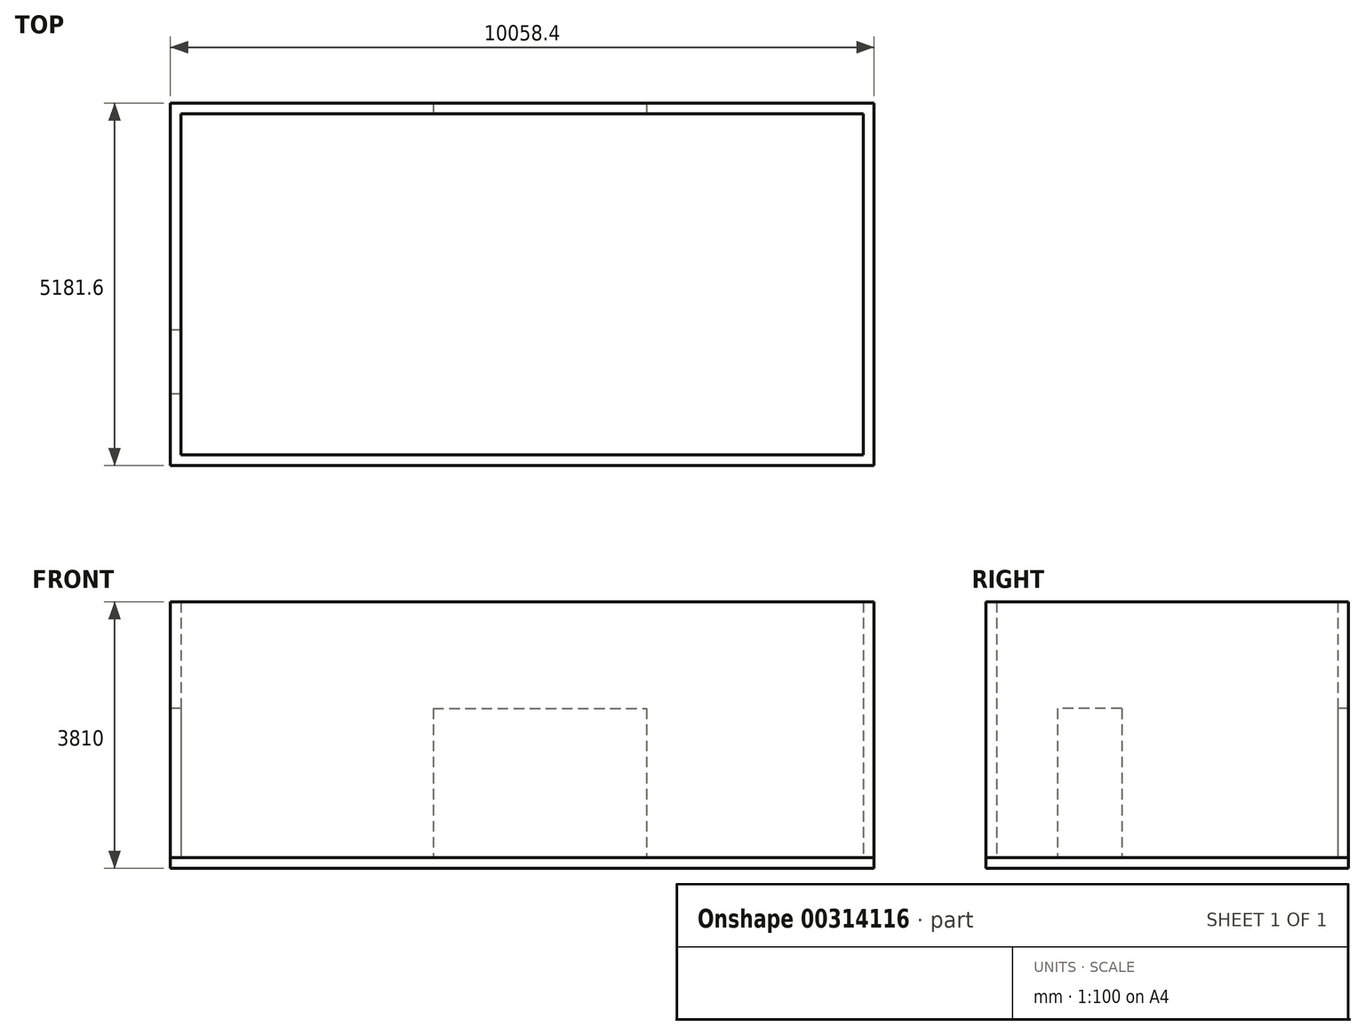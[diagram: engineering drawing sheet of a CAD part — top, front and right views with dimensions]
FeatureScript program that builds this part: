
annotation { "Feature Type Name" : "Feature", "Feature Type Description" : "" }
export const myFeature = defineFeature(function(context is Context, id is Id, definition is map)
    precondition{}
    {
        {
            var Q0;
            Q0=qCreatedBy(makeId("Top.planeOp"),FACE);
            var sketch = newSketch(context, id + "F0", { "sketchPlane" : qUnion([Q0])});
            skLineSegment(sketch, "E0.bottom", {"start": v(-2518.32, 3830.27) * mm, "end": v(7235.28, 3830.27) * mm});
            skLineSegment(sketch, "E0.top", {"start": v(-2518.32, -1046.53) * mm, "end": v(7235.28, -1046.53) * mm});
            skLineSegment(sketch, "E0.left", {"start": v(-2518.32, 3830.27) * mm, "end": v(-2518.32, -1046.53) * mm});
            skLineSegment(sketch, "E0.right", {"start": v(7235.28, 3830.27) * mm, "end": v(7235.28, -1046.53) * mm});
            skLineSegment(sketch, "E1.0", {"start": v(-2670.72, 3982.67) * mm, "end": v(-2670.72, -1198.93) * mm});
            skLineSegment(sketch, "E1.1", {"start": v(-2670.72, 3982.67) * mm, "end": v(7387.68, 3982.67) * mm});
            skLineSegment(sketch, "E1.2", {"start": v(7387.68, 3982.67) * mm, "end": v(7387.68, -1198.93) * mm});
            skLineSegment(sketch, "E1.3", {"start": v(-2670.72, -1198.93) * mm, "end": v(7387.68, -1198.93) * mm});
            skLineSegment(sketch, "E2", {"start": v(-2518.32, 738.17) * mm, "end": v(-2670.72, 738.17) * mm});
            skLineSegment(sketch, "E3", {"start": v(-2518.32, -176.23) * mm, "end": v(-2670.72, -176.23) * mm});
            skLineSegment(sketch, "E4", {"start": v(4132.59, 3982.67) * mm, "end": v(4132.59, 3830.27) * mm});
            skLineSegment(sketch, "E5", {"start": v(1084.59, 3982.67) * mm, "end": v(1084.59, 3830.27) * mm});
            skSolve(sketch);
        }
        {
            var Q0;
            Q0 = qSketchRegion(id + "F0", true);
            extrude(context, id + "F1", {"entities" : qUnion([Q0]), "depth" : 3657.6 * mm});
        }
        {
            var Q0;
            {var subQ0=sQuery(id+"F0.wireOp",EDGE,"E4");Q0=makeQuery(id+"F0.imprint","IMPRINT",FACE,{"disambiguationData":[TD([[makeQuery(id+"F0.imprint","IMPRINT",EDGE,{"derivedFrom":subQ0}),-1.0]])]});}
            var Q1;
            {var subQ0=sQuery(id+"F0.wireOp",EDGE,"E2");Q1=makeQuery(id+"F0.imprint","IMPRINT",FACE,{"disambiguationData":[TD([[makeQuery(id+"F0.imprint","IMPRINT",EDGE,{"derivedFrom":subQ0}),1.0]])]});}
            extrude(context, id + "F2", {"entities" : qUnion([Q0, Q1]), "operationType" : NewBodyOperationType.REMOVE, "depth" : 2133.6 * mm});
        }
        {
            var Q0;
            Q0=makeQuery(id+"F1.opExtrude","CAP_FACE",FACE,{"disambiguationData":[OSD([sQuery(id+"F0.wireOp",EDGE,"E0.bottom"),sQuery(id+"F0.wireOp",EDGE,"E0.top"),sQuery(id+"F0.wireOp",EDGE,"E0.left"),sQuery(id+"F0.wireOp",EDGE,"E0.right"),sQuery(id+"F0.wireOp",EDGE,"E1.0"),sQuery(id+"F0.wireOp",EDGE,"E1.1"),sQuery(id+"F0.wireOp",EDGE,"E1.2"),sQuery(id+"F0.wireOp",EDGE,"E1.3")])],"isStart":true});
            var sketch = newSketch(context, id + "F3", { "sketchPlane" : qUnion([Q0])});
            skLineSegment(sketch, "E6.0", {"start": v(-2670.72, -3982.67) * mm, "end": v(-2670.72, 1198.93) * mm});
            skLineSegment(sketch, "E7.0", {"start": v(-2670.72, -3982.67) * mm, "end": v(7387.68, -3982.67) * mm});
            skLineSegment(sketch, "E8.0", {"start": v(7387.68, -3982.67) * mm, "end": v(7387.68, 1198.93) * mm});
            skLineSegment(sketch, "E9.0", {"start": v(-2670.72, 1198.93) * mm, "end": v(7387.68, 1198.93) * mm});
            skPoint(sketch, "E10.orphan", {"position": v(-2670.72, -738.17) * mm});
            skSolve(sketch);
        }
        {
            var Q0;
            Q0 = qSketchRegion(id + "F3", true);
            extrude(context, id + "F4", {"entities" : qUnion([Q0]), "depth" : 152.4 * mm});
        }
    });
